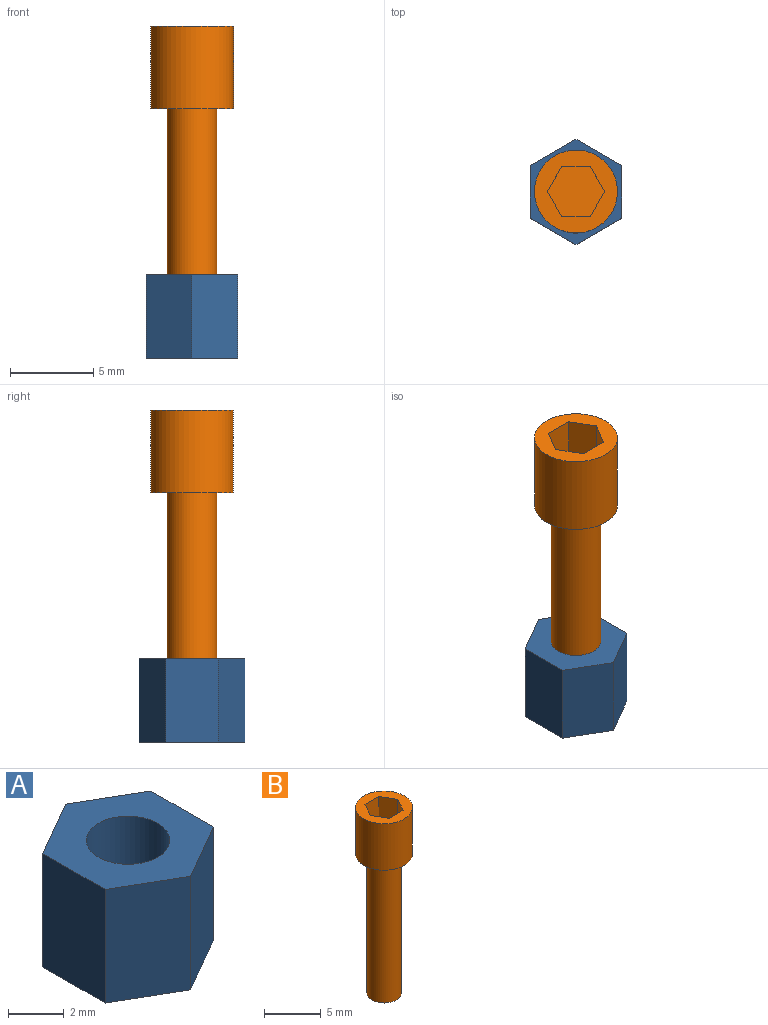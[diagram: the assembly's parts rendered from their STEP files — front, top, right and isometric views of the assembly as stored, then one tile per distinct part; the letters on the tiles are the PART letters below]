
ASSEMBLY  parts=2 mates=1
PART A: 9 faces, bbox 5.5x6.4x5 mm
  f0: plane 5x2.75mm, normal (0.5,0.87,0), area 15.9mm2, adj f1,f6,f7,f8
  f1: plane 5x2.75mm, normal (-0.5,0.87,0), area 15.9mm2, adj f0,f2,f7,f8
  f2: plane 5x3.18mm, normal (-1,0,0), area 15.9mm2, adj f1,f3,f7,f8
  f3: plane 5x2.75mm, normal (-0.5,-0.87,0), area 15.9mm2, adj f2,f4,f7,f8
  f4: plane 5x2.75mm, normal (0.5,-0.87,0), area 15.9mm2, adj f3,f6,f7,f8
  f5: cylinder r=1.5mm len=5mm, axis (0,0,-1), area 47.1mm2, adj f7,f8
  f6: plane 5x3.18mm, normal (1,0,0), area 15.9mm2, adj f0,f4,f7,f8
  f7: plane 6.35x5.5mm, normal (0,0,1), area 19.1mm2, adj f0,f1,f2,f3,f4,f5,f6
  f8: plane 6.35x5.5mm, normal (0,0,-1), area 19.1mm2, adj f0,f1,f2,f3,f4,f5,f6
PART B: 12 faces, bbox 5x5x20 mm
  f0: plane 5x5mm, normal (0,0,1), area 11.8mm2, adj f3,f5,f6,f7,f8,f9,f10
  f1: cylinder r=1.5mm len=15mm, axis (0,0,1), area 141.4mm2, adj f2,f4
  f2: plane 3x3mm, normal (0,0,-1), area 7.1mm2, adj f1
  f3: cylinder r=2.5mm len=5mm, axis (0,0,-1), area 78.5mm2, adj f0,f4
  f4: plane 5x5mm, normal (0,0,-1), area 12.6mm2, adj f1,f3
  f5: plane 3x1.5mm, normal (0.87,0.5,0), area 5.2mm2, adj f0,f6,f10,f11
  f6: plane 3x1.73mm, normal (0,1,0), area 5.2mm2, adj f0,f5,f7,f11
  f7: plane 3x1.5mm, normal (-0.87,0.5,0), area 5.2mm2, adj f0,f6,f8,f11
  f8: plane 3x1.5mm, normal (-0.87,-0.5,0), area 5.2mm2, adj f0,f7,f9,f11
  f9: plane 3x1.73mm, normal (0,-1,0), area 5.2mm2, adj f0,f8,f10,f11
  f10: plane 3x1.5mm, normal (0.87,-0.5,0), area 5.2mm2, adj f0,f5,f9,f11
  f11: plane 3.46x3mm, normal (0,0,1), area 7.8mm2, adj f5,f6,f7,f8,f9,f10
PLACE A t=(0,0,-15)mm
PLACE B at identity
MATE fastened A.f5 <-> B.f1  axis (0,0,-1) through (0,0,-15)mm
